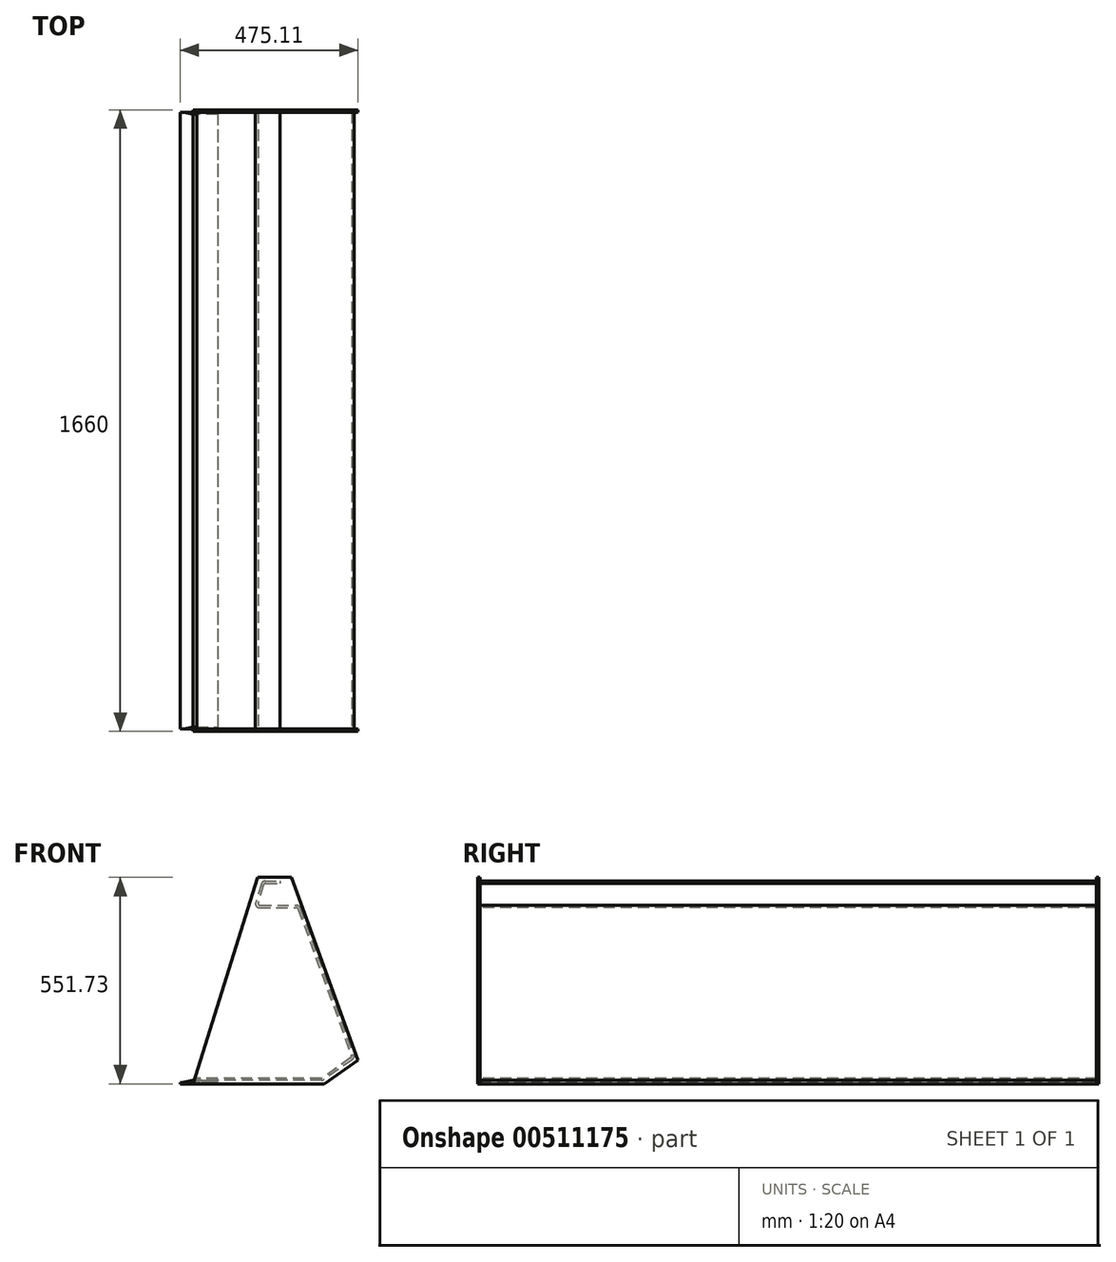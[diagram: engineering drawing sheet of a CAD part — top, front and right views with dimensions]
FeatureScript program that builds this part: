
annotation { "Feature Type Name" : "Feature", "Feature Type Description" : "" }
export const myFeature = defineFeature(function(context is Context, id is Id, definition is map)
    precondition{}
    {
        {
            var Q0;
            Q0=qCreatedBy(makeId("Front.planeOp"),FACE);
            var sketch = newSketch(context, id + "F0", { "sketchPlane" : qUnion([Q0])});
            skLineSegment(sketch, "E0", {"start": v(0, 0) * mm, "end": v(350, 0) * mm});
            skLineSegment(sketch, "E1", {"start": v(350, 0) * mm, "end": v(440.1, 63.1) * mm});
            skLineSegment(sketch, "E2", {"start": v(440.1, 63.1) * mm, "end": v(262.26, 551.73) * mm});
            skLineSegment(sketch, "E3", {"start": v(262.26, 551.73) * mm, "end": v(172.26, 551.73) * mm});
            skLineSegment(sketch, "E4", {"start": v(172.26, 551.73) * mm, "end": v(0, 0) * mm});
            skLineSegment(sketch, "E5", {"start": v(350, 0) * mm, "end": v(443.7, 0) * mm, "construction": true});
            skLineSegment(sketch, "E6", {"start": v(440.1, 63.1) * mm, "end": v(469.76, -18.39) * mm, "construction": true});
            skLineSegment(sketch, "E7", {"start": v(262.26, 551.73) * mm, "end": v(338.42, 551.73) * mm, "construction": true});
            skSolve(sketch);
        }
        {
            var Q0;
            Q0=makeQuery(id+"F0.imprint","IMPRINT",FACE,{"disambiguationData":[TD([[makeQuery(id+"F0.imprint","IMPRINT",EDGE,{"derivedFrom":sQuery(id+"F0.wireOp",EDGE,"E0")}),1.0]])]});
            extrude(context, id + "F1", {"entities" : qUnion([Q0]), "depth" : 6 * mm});
        }
        {
            var Q0;
            Q0=qCreatedBy(makeId("Front.planeOp"),FACE);
            var sketch = newSketch(context, id + "F2", { "sketchPlane" : qUnion([Q0])});
            skLineSegment(sketch, "E8", {"start": v(192.2, 541.73) * mm, "end": v(232.26, 541.73) * mm});
            skLineSegment(sketch, "E9", {"start": v(182.66, 534.71) * mm, "end": v(166.73, 483.71) * mm});
            skLineSegment(sketch, "E10", {"start": v(285.56, 470.15) * mm, "end": v(428.85, 76.47) * mm});
            skLineSegment(sketch, "E11", {"start": v(425.2, 64.86) * mm, "end": v(349.43, 11.8) * mm});
            skLineSegment(sketch, "E12", {"start": v(343.7, 10) * mm, "end": v(10, 10) * mm});
            skLineSegment(sketch, "E13.0", {"start": v(193.67, 535.73) * mm, "end": v(232.26, 535.73) * mm});
            skLineSegment(sketch, "E14.0", {"start": v(187.95, 531.52) * mm, "end": v(173.27, 484.52) * mm});
            skLineSegment(sketch, "E15.0", {"start": v(179, 476.73) * mm, "end": v(276.17, 476.73) * mm});
            skLineSegment(sketch, "E16.0", {"start": v(280.4, 466.79) * mm, "end": v(422.7, 75.86) * mm});
            skLineSegment(sketch, "E17.0", {"start": v(420.5, 68.9) * mm, "end": v(344.96, 16) * mm});
            skLineSegment(sketch, "E18", {"start": v(10, 0) * mm, "end": v(10, 114.42) * mm, "construction": true});
            skLineSegment(sketch, "E19", {"start": v(341.51, 14.91) * mm, "end": v(10, 14.91) * mm});
            skLineSegment(sketch, "E20", {"start": v(10, 14.91) * mm, "end": v(10, 10) * mm});
            skLineSegment(sketch, "E21", {"start": v(176.28, 470.73) * mm, "end": v(274.77, 470.73) * mm});
            skLineSegment(sketch, "E22", {"start": v(232.26, 541.73) * mm, "end": v(232.26, 535.73) * mm});
            skPoint(sketch, "E23.visualSharp", {"position": v(189.26, 535.73) * mm});
            skArc(sketch, "E23.filletArc", {"start": v(193.67, 535.73) * mm, "mid": v(190.12, 534.57) * mm, "end": v(187.95, 531.52) * mm});
            skPoint(sketch, "E24.visualSharp", {"position": v(184.85, 541.73) * mm});
            skArc(sketch, "E24.filletArc", {"start": v(192.2, 541.73) * mm, "mid": v(186.28, 539.79) * mm, "end": v(182.66, 534.71) * mm});
            skPoint(sketch, "E25.visualSharp", {"position": v(170.84, 476.73) * mm});
            skArc(sketch, "E25.filletArc", {"start": v(173.27, 484.52) * mm, "mid": v(174.17, 479.18) * mm, "end": v(179, 476.73) * mm});
            skPoint(sketch, "E26.visualSharp", {"position": v(162.68, 470.73) * mm});
            skArc(sketch, "E26.filletArc", {"start": v(166.73, 483.71) * mm, "mid": v(168.22, 474.8) * mm, "end": v(176.28, 470.73) * mm});
            skPoint(sketch, "E27.visualSharp", {"position": v(283.17, 476.73) * mm});
            skArc(sketch, "E27.filletArc", {"start": v(285.56, 470.15) * mm, "mid": v(281.9, 474.93) * mm, "end": v(276.17, 476.73) * mm});
            skPoint(sketch, "E28.visualSharp", {"position": v(278.97, 470.73) * mm});
            skArc(sketch, "E28.filletArc", {"start": v(280.4, 466.79) * mm, "mid": v(278.2, 469.65) * mm, "end": v(274.77, 470.73) * mm});
            skPoint(sketch, "E29.visualSharp", {"position": v(424.26, 71.53) * mm});
            skArc(sketch, "E29.filletArc", {"start": v(420.5, 68.9) * mm, "mid": v(422.77, 72) * mm, "end": v(422.7, 75.86) * mm});
            skPoint(sketch, "E30.visualSharp", {"position": v(431.48, 69.26) * mm});
            skArc(sketch, "E30.filletArc", {"start": v(425.2, 64.86) * mm, "mid": v(429, 70.04) * mm, "end": v(428.85, 76.47) * mm});
            skPoint(sketch, "E31.visualSharp", {"position": v(346.85, 10) * mm});
            skArc(sketch, "E31.filletArc", {"start": v(343.7, 10) * mm, "mid": v(346.7, 10.46) * mm, "end": v(349.43, 11.8) * mm});
            skPoint(sketch, "E32.visualSharp", {"position": v(343.4, 14.91) * mm});
            skArc(sketch, "E32.filletArc", {"start": v(341.51, 14.91) * mm, "mid": v(343.32, 15.2) * mm, "end": v(344.96, 16) * mm});
            skLineSegment(sketch, "E33.bottom", {"start": v(-35, 0) * mm, "end": v(65, 0) * mm});
            skLineSegment(sketch, "E33.top", {"start": v(-35, 10) * mm, "end": v(65, 10) * mm});
            skLineSegment(sketch, "E33.left", {"start": v(-35, 0) * mm, "end": v(-35, 10) * mm});
            skLineSegment(sketch, "E33.right", {"start": v(65, 0) * mm, "end": v(65, 10) * mm});
            skSolve(sketch);
        }
        {
            var Q0;
            Q0=makeQuery(id+"F2.imprint","IMPRINT",FACE,{"disambiguationData":[TD([[makeQuery(id+"F2.imprint","IMPRINT",EDGE,{"derivedFrom":sQuery(id+"F2.wireOp",EDGE,"E8")}),-1.0]])]});
            extrude(context, id + "F3", {"entities" : qUnion([Q0]), "oppositeDirection" : true, "depth" : 1648 * mm});
        }
        {
            var Q0;
            Q0=makeQuery(id+"F1.opExtrude","CAP_FACE",FACE,{"disambiguationData":[OSD([sQuery(id+"F0.wireOp",EDGE,"E0"),sQuery(id+"F0.wireOp",EDGE,"E1"),sQuery(id+"F0.wireOp",EDGE,"E2"),sQuery(id+"F0.wireOp",EDGE,"E3"),sQuery(id+"F0.wireOp",EDGE,"E4")])],"isStart":true});
            cPlane(context, id + "F4", {"entities" : qUnion([Q0]), "cplaneType" : CPlaneType.OFFSET, "offset" : 824 * mm, "width" : 150 * mm, "height" : 150 * mm});
        }
        {
            var Q0;
            Q0=makeQuery(id+"F1.opExtrude","SWEPT_BODY",BODY,{"disambiguationData":[OSD([sQuery(id+"F0.wireOp",EDGE,"E0"),sQuery(id+"F0.wireOp",EDGE,"E1"),sQuery(id+"F0.wireOp",EDGE,"E2"),sQuery(id+"F0.wireOp",EDGE,"E3"),sQuery(id+"F0.wireOp",EDGE,"E4")])]});
            var Q1;
            Q1=qCreatedBy(id+"F4.planeOp",FACE);
            mirror(context, id + "F5", {"entities" : qUnion([Q0]), "mirrorPlane" : qUnion([Q1])});
        }
        {
            var Q0;
            Q0=makeQuery(id+"F2.imprint","IMPRINT",FACE,{"disambiguationData":[TD([[makeQuery(id+"F2.imprint","IMPRINT",EDGE,{"derivedFrom":sQuery(id+"F2.wireOp",EDGE,"E33.bottom")}),1.0]])]});
            extrude(context, id + "F6", {"entities" : qUnion([Q0]), "oppositeDirection" : true, "depth" : 1648 * mm});
        }
        {
            var Q0;
            Q0=makeQuery(id+"F6.opExtrude","SWEPT_EDGE",EDGE,{"disambiguationData":[OSD([sQuery(id+"F2.wireOp",EDGE,"E33.top"),sQuery(id+"F2.wireOp",EDGE,"E33.left")])]});
            chamfer(context, id + "F7", {"entities" : qUnion([Q0]), "chamferType" : ChamferType.TWO_OFFSETS, "width1" : 35 * mm, "oppositeDirection" : false, "width2" : 7 * mm, "tangentPropagation" : true});
        }
        {
            var Q0;
            Q0=makeQuery(id+"F6.opExtrude","CAP_EDGE",EDGE,{"disambiguationData":[OSD([sQuery(id+"F2.wireOp",EDGE,"E33.top")])],"isStart":true});
            var Q1;
            Q1=makeQuery(id+"F6.opExtrude","CAP_EDGE",EDGE,{"disambiguationData":[OSD([sQuery(id+"F2.wireOp",EDGE,"E33.top")])],"isStart":false});
            chamfer(context, id + "F8", {"entities" : qUnion([Q0, Q1]), "width" : 5 * mm, "tangentPropagation" : true});
        }
    });
